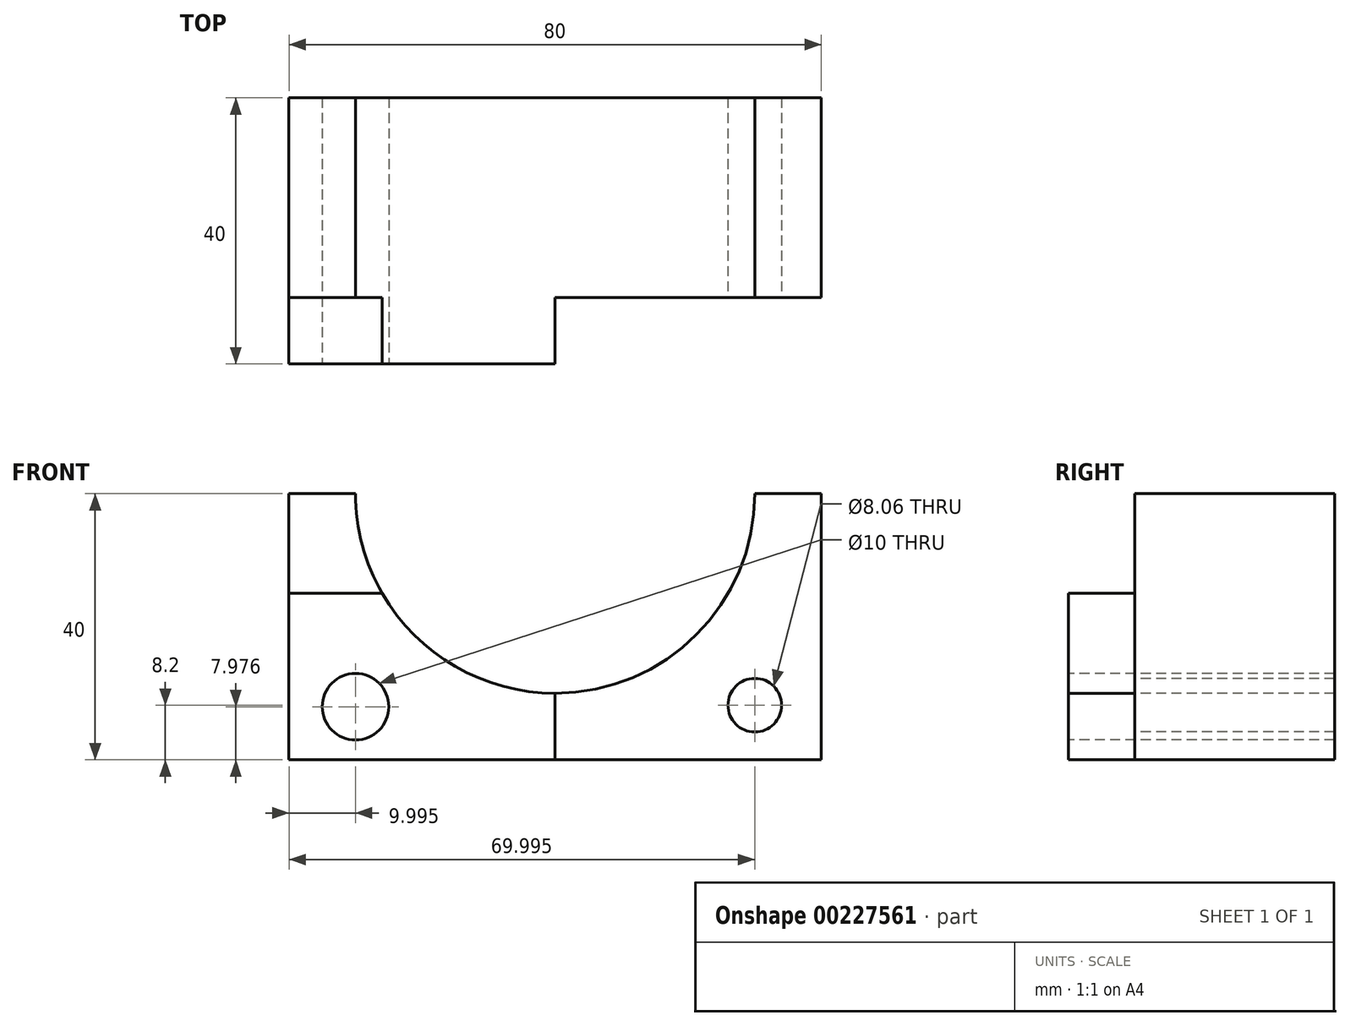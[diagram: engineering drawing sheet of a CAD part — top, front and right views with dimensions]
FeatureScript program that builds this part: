
annotation { "Feature Type Name" : "Feature", "Feature Type Description" : "" }
export const myFeature = defineFeature(function(context is Context, id is Id, definition is map)
    precondition{}
    {
        {
            var Q0;
            Q0=qCreatedBy(makeId("Top.planeOp"),FACE);
            var sketch = newSketch(context, id + "F0", { "sketchPlane" : qUnion([Q0])});
            skLineSegment(sketch, "E0.bottom", {"start": v(-38.98, 22.08) * mm, "end": v(41.02, 22.08) * mm});
            skLineSegment(sketch, "E0.top", {"start": v(-38.98, -17.92) * mm, "end": v(1.02, -17.92) * mm});
            skLineSegment(sketch, "E0.left", {"start": v(-38.98, 22.08) * mm, "end": v(-38.98, -17.92) * mm});
            skLineSegment(sketch, "E0.right", {"start": v(41.02, 22.08) * mm, "end": v(41.02, -7.92) * mm});
            skLineSegment(sketch, "E1", {"start": v(41.02, -7.92) * mm, "end": v(1.02, -7.92) * mm});
            skLineSegment(sketch, "E2", {"start": v(1.02, -7.92) * mm, "end": v(1.02, -17.92) * mm});
            skSolve(sketch);
        }
        {
            var Q0;
            Q0=makeQuery(id+"F0.imprint","IMPRINT",FACE,{"disambiguationData":[TD([[makeQuery(id+"F0.imprint","IMPRINT",EDGE,{"derivedFrom":sQuery(id+"F0.wireOp",EDGE,"E0.bottom")}),-1.0]])]});
            extrude(context, id + "F1", {"entities" : qUnion([Q0]), "depth" : 40 * mm});
        }
        {
            var Q0;
            Q0=makeQuery(id+"F1.opExtrude","SWEPT_FACE",FACE,{"disambiguationData":[OSD([sQuery(id+"F0.wireOp",EDGE,"E0.top")])]});
            var sketch = newSketch(context, id + "F2", { "sketchPlane" : qUnion([Q0])});
            skCircle(sketch, "E3", {"center": v(-28.98, 7.98) * mm, "radius": 5 * mm});
            skCircle(sketch, "E4", {"center": v(31.02, 8.2) * mm, "radius": 4.03 * mm});
            skPoint(sketch, "E5", {"position": v(1.02, 40) * mm});
            skCircle(sketch, "E6", {"center": v(1.02, 40) * mm, "radius": 30 * mm});
            skLineSegment(sketch, "E7.bottom", {"start": v(-41.95, 45) * mm, "end": v(-24.97, 45) * mm});
            skLineSegment(sketch, "E7.top", {"start": v(-41.95, 25) * mm, "end": v(-24.97, 25) * mm});
            skLineSegment(sketch, "E7.left", {"start": v(-41.95, 45) * mm, "end": v(-41.95, 25) * mm});
            skLineSegment(sketch, "E7.right", {"start": v(-24.97, 45) * mm, "end": v(-24.97, 25) * mm});
            skSolve(sketch);
        }
        {
            var Q0;
            {var subQ6=sQuery(id+"F2.wireOp",EDGE,"E7.right");var subQ7=sQuery(id+"F2.wireOp",EDGE,"E7.bottom");var subQ8=makeQuery(id+"F2.imprint","INTERSECT",VERTEX,{"derivedFrom":[subQ7,subQ6]});Q0=makeQuery(id+"F2.imprint","IMPRINT",FACE,{"disambiguationData":[TD([[makeQuery(id+"F2.imprint","IMPRINT",EDGE,{"disambiguationData":[TD([[subQ8,1.0]])],"derivedFrom":subQ7}),1.0]])]});}
            var Q1;
            {var subQ0=sQuery(id+"F2.wireOp",EDGE,"E7.right");var subQ3=sQuery(id+"F0.wireOp",EDGE,"E0.top");var subQ6=makeQuery(id+"F1.opExtrude","CAP_EDGE",EDGE,{"disambiguationData":[OSD([subQ3])],"isStart":false});var subQ7=makeQuery(id+"F2.imprint","INTERSECT",VERTEX,{"derivedFrom":[subQ6,subQ0]});Q1=makeQuery(id+"F2.imprint","IMPRINT",FACE,{"disambiguationData":[TD([[makeQuery(id+"F2.imprint","IMPRINT",EDGE,{"disambiguationData":[TD([[subQ7,-1.0]])],"derivedFrom":subQ0}),1.0]])]});}
            var Q2;
            {var subQ1=sQuery(id+"F2.wireOp",EDGE,"E6");var subQ3=makeQuery(id+"F1.opExtrude","CAP_EDGE",EDGE,{"disambiguationData":[OSD([sQuery(id+"F0.wireOp",EDGE,"E0.top")])],"isStart":false});var subQ4=makeQuery(id+"F2.imprint","INTERSECT",VERTEX,{"derivedFrom":[subQ3,subQ1]});Q2=makeQuery(id+"F2.imprint","IMPRINT",FACE,{"disambiguationData":[TD([[makeQuery(id+"F2.imprint","IMPRINT",EDGE,{"disambiguationData":[TD([[subQ4,-1.0]])],"derivedFrom":subQ3}),-1.0]])]});}
            var Q3;
            Q3=makeQuery(id+"F2.imprint","IMPRINT",FACE,{"disambiguationData":[TD([[makeQuery(id+"F2.imprint","IMPRINT",EDGE,{"derivedFrom":sQuery(id+"F2.wireOp",EDGE,"E3")}),1.0]])]});
            var Q4;
            Q4=makeQuery(id+"F2.imprint","IMPRINT",FACE,{"disambiguationData":[TD([[makeQuery(id+"F2.imprint","IMPRINT",EDGE,{"derivedFrom":sQuery(id+"F2.wireOp",EDGE,"E4")}),1.0]])]});
            var Q5;
            {var subQ0=sQuery(id+"F2.wireOp",EDGE,"E7.bottom");var subQ1=sQuery(id+"F2.wireOp",EDGE,"E6");var subQ2=makeQuery(id+"F2.imprint","INTERSECT",VERTEX,{"derivedFrom":[subQ1,subQ0]});Q5=makeQuery(id+"F2.imprint","IMPRINT",FACE,{"disambiguationData":[TD([[makeQuery(id+"F2.imprint","IMPRINT",EDGE,{"disambiguationData":[TD([[subQ2,-1.0]])],"derivedFrom":subQ1}),1.0]])]});}
            extrude(context, id + "F3", {"entities" : qUnion([Q0, Q1, Q2, Q3, Q4, Q5]), "operationType" : NewBodyOperationType.REMOVE, "endBound" : BoundingType.THROUGH_ALL, "oppositeDirection" : true, "depth" : 25 * mm});
        }
        {
            var Q0;
            Q0=makeQuery(id+"F1.opExtrude","SWEPT_FACE",FACE,{"disambiguationData":[OSD([sQuery(id+"F0.wireOp",EDGE,"E0.top")])]});
            var sketch = newSketch(context, id + "F4", { "sketchPlane" : qUnion([Q0])});
            skLineSegment(sketch, "E8.bottom", {"start": v(-45.8, 48.6) * mm, "end": v(-19.92, 48.6) * mm});
            skLineSegment(sketch, "E8.top", {"start": v(-45.8, 25) * mm, "end": v(-19.92, 25) * mm});
            skLineSegment(sketch, "E8.left", {"start": v(-45.8, 48.6) * mm, "end": v(-45.8, 25) * mm});
            skLineSegment(sketch, "E8.right", {"start": v(-19.92, 48.6) * mm, "end": v(-19.92, 25) * mm});
            skSolve(sketch);
        }
        {
            var Q0;
            Q0=makeQuery(id+"F4.imprint","IMPRINT",FACE,{"disambiguationData":[TD([[makeQuery(id+"F4.imprint","IMPRINT",EDGE,{"derivedFrom":sQuery(id+"F4.wireOp",EDGE,"E8.bottom")}),-1.0]])]});
            var Q1;
            {var subQ1=sQuery(id+"F0.wireOp",EDGE,"E0.top");var subQ6=makeQuery(id+"F1.opExtrude","CAP_EDGE",EDGE,{"disambiguationData":[OSD([subQ1])],"isStart":false});Q1=makeQuery(id+"F4.imprint","IMPRINT",FACE,{"disambiguationData":[TD([[makeQuery(id+"F4.imprint","IMPRINT",EDGE,{"derivedFrom":subQ6}),-1.0]])]});}
            extrude(context, id + "F5", {"entities" : qUnion([Q0, Q1]), "operationType" : NewBodyOperationType.REMOVE, "oppositeDirection" : true, "depth" : 10 * mm});
        }
    });
